# Revit family: Haworth_BandasSpace_Lounge
name_source: partatom
category: Furniture
revit_build: Autodesk Revit 2018 (Build: 20170223_1515(x64)
units: mm (PartAtom-declared; Revit-internal decimal feet)

## family parameters
Always vertical = Yes
Cut with Voids When Loaded = No
OmniClass Number = 23.35.50.27.11.11
OmniClass Title = Access Floors, Frames
Room Calculation Point = No
Shared = No
Work Plane-Based = No

## types (2) — shared parameters
Actual Height = 23 77/128"
Actual Width = 23 77/128"
Manufacturer = Haworth
Model = HCGN-BNL
Note = Verify Final Dimensions w/ Haworth
Revision Number = 1
Seat Finish Inner = Haworth _ Wool _ Bandas Space
Seat Height = 13 3/4"
URL = http://www.haworth.com
URL - Product = https://www.haworth.com
Warranty = http://www.haworth.com

## per-type parameters (varying)
| type | Actual Depth | Description | Large | Small |
| HCGN-BNL1 - Lounge Chair | 37 51/128" | Haworth - Bandas Space - Lounge Chair | No | Yes |
| HCGN-BNLC - Chaise Lounge | 61" | Haworth - Bandas Space - Chaise Lounge | Yes | No |

## geometry (parser evidence)
native form markers: Sweep x3
no freeform markers — native parametric forms only
